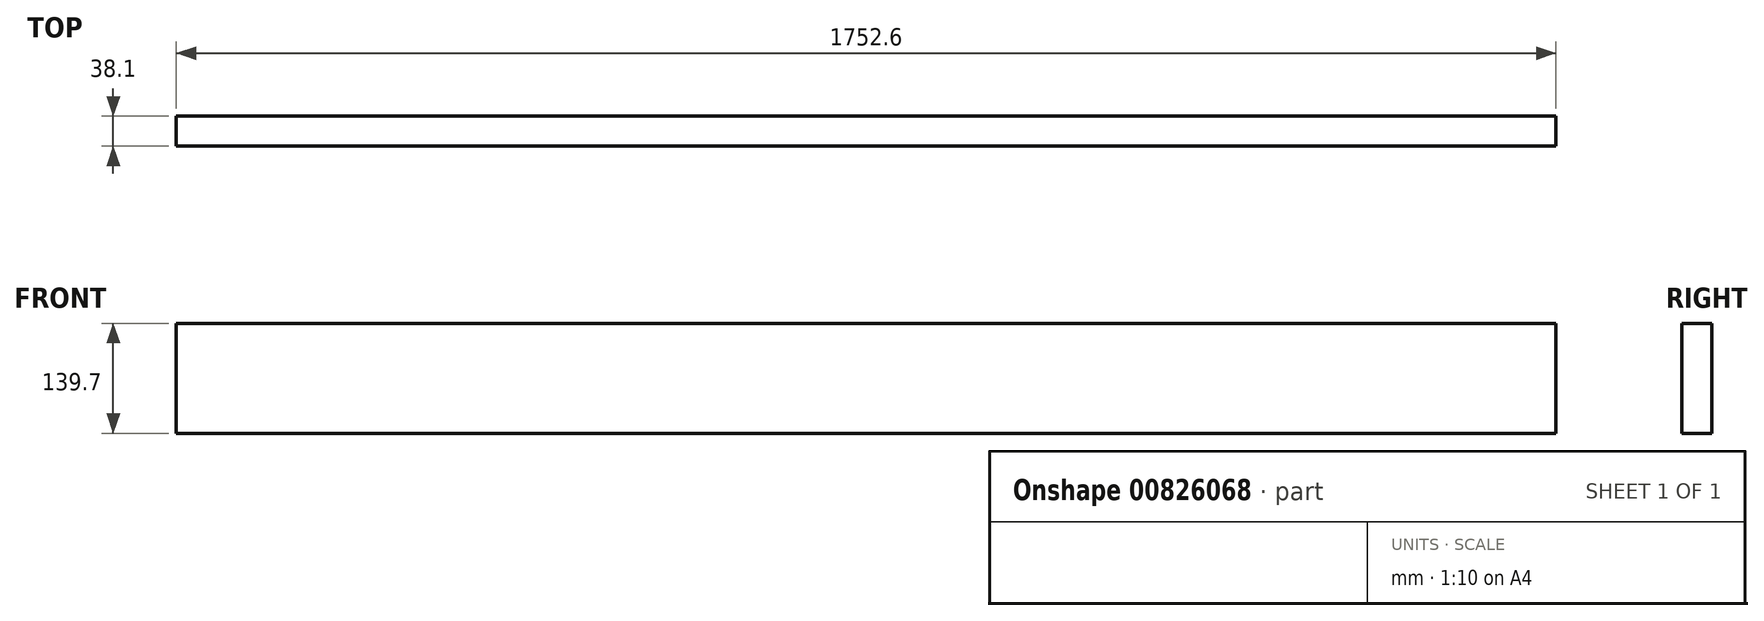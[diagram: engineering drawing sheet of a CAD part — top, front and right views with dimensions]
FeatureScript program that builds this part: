
annotation { "Feature Type Name" : "Feature", "Feature Type Description" : "" }
export const myFeature = defineFeature(function(context is Context, id is Id, definition is map)
    precondition{}
    {
        {
            var Q0;
            Q0=qCreatedBy(makeId("Front.planeOp"),FACE);
            var sketch = newSketch(context, id + "F0", { "sketchPlane" : qUnion([Q0])});
            skLineSegment(sketch, "E0.bottom", {"start": v(0, 0) * mm, "end": v(1752.6, 0) * mm});
            skLineSegment(sketch, "E0.top", {"start": v(0, 139.7) * mm, "end": v(1752.6, 139.7) * mm});
            skLineSegment(sketch, "E0.left", {"start": v(0, 0) * mm, "end": v(0, 139.7) * mm});
            skLineSegment(sketch, "E0.right", {"start": v(1752.6, 0) * mm, "end": v(1752.6, 139.7) * mm});
            skSolve(sketch);
        }
        {
            var Q0;
            Q0=makeQuery(id+"F0.imprint","IMPRINT",FACE,{"disambiguationData":[TD([[makeQuery(id+"F0.imprint","IMPRINT",EDGE,{"derivedFrom":sQuery(id+"F0.wireOp",EDGE,"E0.bottom")}),1.0]])]});
            extrude(context, id + "F1", {"entities" : qUnion([Q0]), "depth" : 38.1 * mm, "offsetDistance" : 25.4 * mm});
        }
    });
